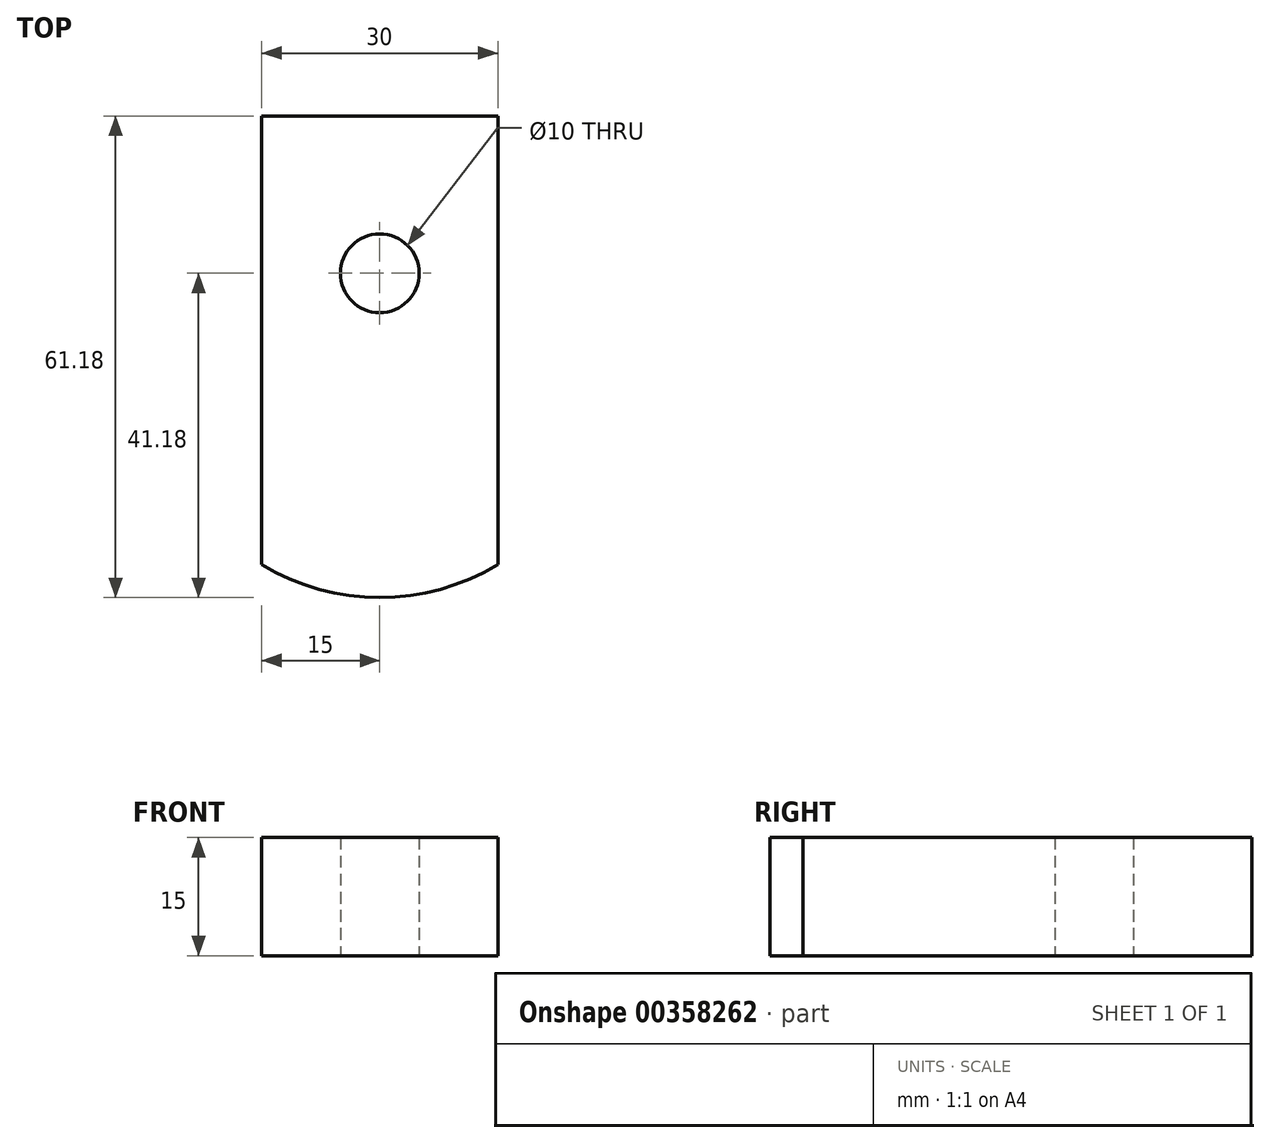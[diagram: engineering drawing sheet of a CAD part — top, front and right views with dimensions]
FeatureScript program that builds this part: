
annotation { "Feature Type Name" : "Feature", "Feature Type Description" : "" }
export const myFeature = defineFeature(function(context is Context, id is Id, definition is map)
    precondition{}
    {
        {
            var Q0;
            Q0=qCreatedBy(makeId("Top.planeOp"),FACE);
            var sketch = newSketch(context, id + "F0", { "sketchPlane" : qUnion([Q0])});
            skCircle(sketch, "E0", {"center": v(0, 0) * mm, "radius": 5 * mm});
            skLineSegment(sketch, "E1.bottom", {"start": v(15, 20) * mm, "end": v(-15, 20) * mm});
            skLineSegment(sketch, "E1.left", {"start": v(15, 20) * mm, "end": v(15, -37) * mm});
            skLineSegment(sketch, "E1.right", {"start": v(-15, 20) * mm, "end": v(-15, -37) * mm});
            skArc(sketch, "E2", {"start": v(-15, -37) * mm, "mid": v(0, -41.18) * mm, "end": v(15, -37) * mm});
            skSolve(sketch);
        }
        {
            var Q0;
            Q0 = qSketchRegion(id + "F0", true);
            extrude(context, id + "F1", {"entities" : qUnion([Q0]), "depth" : 15 * mm});
        }
    });
